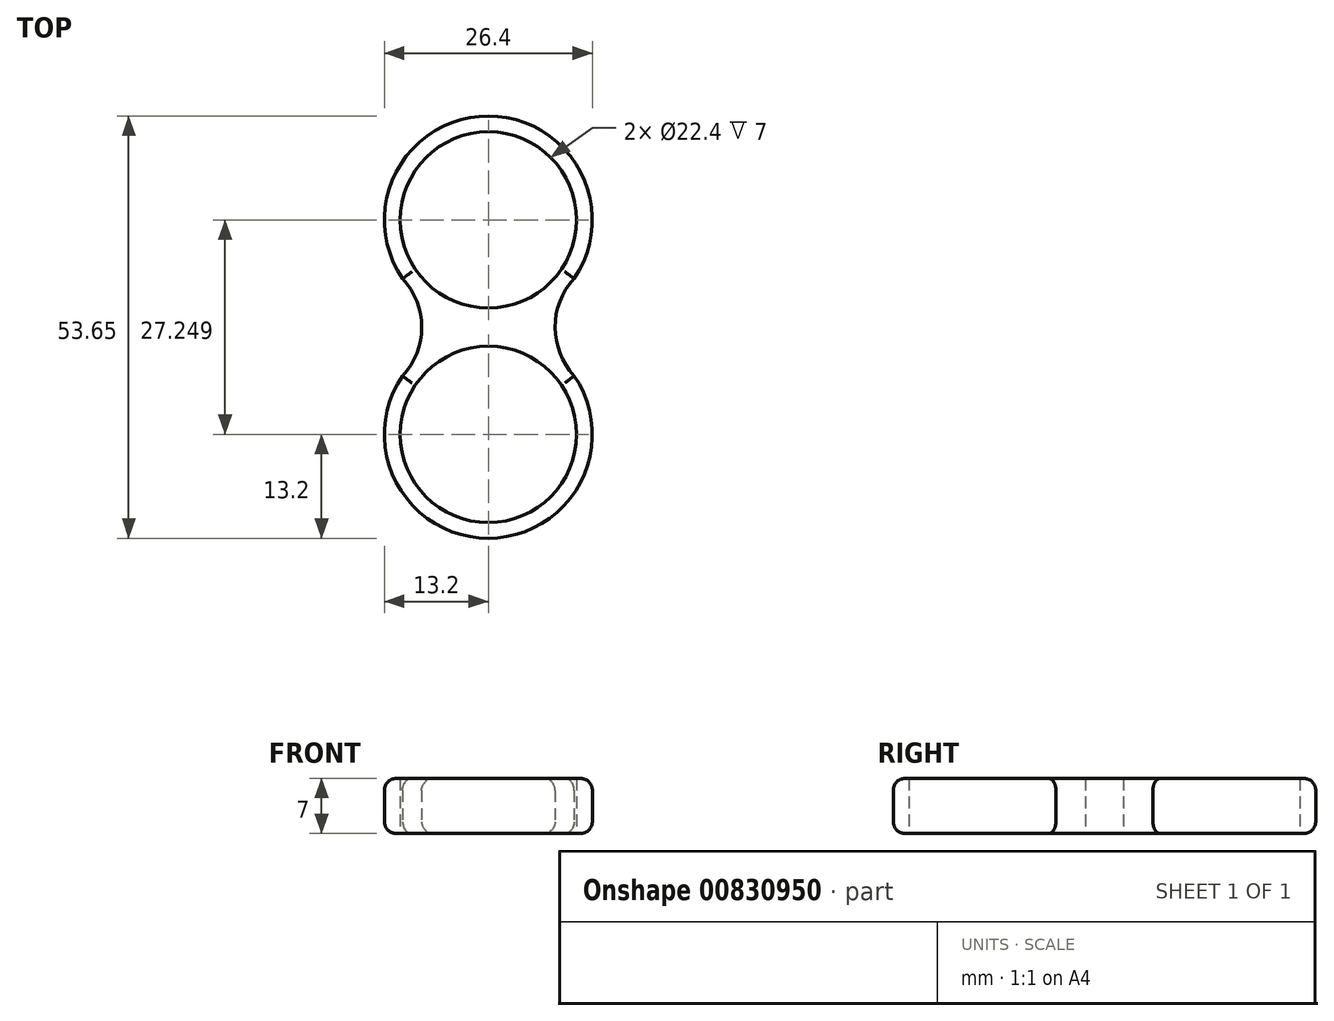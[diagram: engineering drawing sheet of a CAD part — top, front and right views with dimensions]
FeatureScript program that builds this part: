
annotation { "Feature Type Name" : "Feature", "Feature Type Description" : "" }
export const myFeature = defineFeature(function(context is Context, id is Id, definition is map)
    precondition{}
    {
        {
            var Q0;
            Q0=qCreatedBy(makeId("Top.planeOp"),FACE);
            var sketch = newSketch(context, id + "F0", { "sketchPlane" : qUnion([Q0])});
            skCircle(sketch, "E0", {"center": v(0, 0) * mm, "radius": 11.2 * mm});
            skArc(sketch, "E1", {"start": v(-9.91, 8.71) * mm, "mid": v(0, -13.2) * mm, "end": v(9.91, 8.71) * mm});
            skCircle(sketch, "E2", {"center": v(0, 27.25) * mm, "radius": 11.2 * mm});
            skArc(sketch, "E3", {"start": v(9.93, 18.56) * mm, "mid": v(0, 40.45) * mm, "end": v(-9.93, 18.56) * mm});
            skArc(sketch, "E4", {"start": v(-10.9, 7.45) * mm, "mid": v(-8.47, 13.6) * mm, "end": v(-10.88, 19.77) * mm});
            skArc(sketch, "E5.MirrorCS", {"start": v(10.9, 7.45) * mm, "mid": v(8.47, 13.6) * mm, "end": v(10.88, 19.77) * mm});
            skSolve(sketch);
        }
        {
            var Q0;
            Q0=makeQuery(id+"F0.imprint","IMPRINT",FACE,{"disambiguationData":[TD([[makeQuery(id+"F0.imprint","IMPRINT",EDGE,{"derivedFrom":sQuery(id+"F0.wireOp",EDGE,"E0")}),-1.0]])]});
            extrude(context, id + "F1", {"entities" : qUnion([Q0]), "depth" : 7 * mm, "offsetDistance" : 25 * mm});
        }
        {
            var Q0;
            Q0=makeQuery(id+"F1.opExtrude","CAP_EDGE",EDGE,{"disambiguationData":[OSD([sQuery(id+"F0.wireOp",EDGE,"E1")])],"isStart":false});
            var Q1;
            Q1=makeQuery(id+"F1.opExtrude","CAP_EDGE",EDGE,{"disambiguationData":[OSD([sQuery(id+"F0.wireOp",EDGE,"E3")])],"isStart":false});
            var Q2;
            Q2=makeQuery(id+"F1.opExtrude","CAP_EDGE",EDGE,{"disambiguationData":[OSD([sQuery(id+"F0.wireOp",EDGE,"E4")])],"isStart":false});
            var Q3;
            Q3=makeQuery(id+"F1.opExtrude","CAP_EDGE",EDGE,{"disambiguationData":[OSD([sQuery(id+"F0.wireOp",EDGE,"E5.MirrorCS")])],"isStart":false});
            fillet(context, id + "F2", {"entities" : qUnion([Q0, Q1, Q2, Q3]), "radius" : 1.5 * mm, "tangentPropagation" : true, "allowEdgeOverflow" : false});
        }
        {
            var Q0;
            Q0=makeQuery(id+"F1.opExtrude","CAP_EDGE",EDGE,{"disambiguationData":[OSD([sQuery(id+"F0.wireOp",EDGE,"E1")])],"isStart":true});
            var Q1;
            Q1=makeQuery(id+"F1.opExtrude","CAP_EDGE",EDGE,{"disambiguationData":[OSD([sQuery(id+"F0.wireOp",EDGE,"E3")])],"isStart":true});
            var Q2;
            Q2=makeQuery(id+"F1.opExtrude","CAP_EDGE",EDGE,{"disambiguationData":[OSD([sQuery(id+"F0.wireOp",EDGE,"E4")])],"isStart":true});
            var Q3;
            Q3=makeQuery(id+"F1.opExtrude","CAP_EDGE",EDGE,{"disambiguationData":[OSD([sQuery(id+"F0.wireOp",EDGE,"E5.MirrorCS")])],"isStart":true});
            fillet(context, id + "F3", {"entities" : qUnion([Q0, Q1, Q2, Q3]), "radius" : 1.5 * mm, "tangentPropagation" : true, "allowEdgeOverflow" : false});
        }
    });
